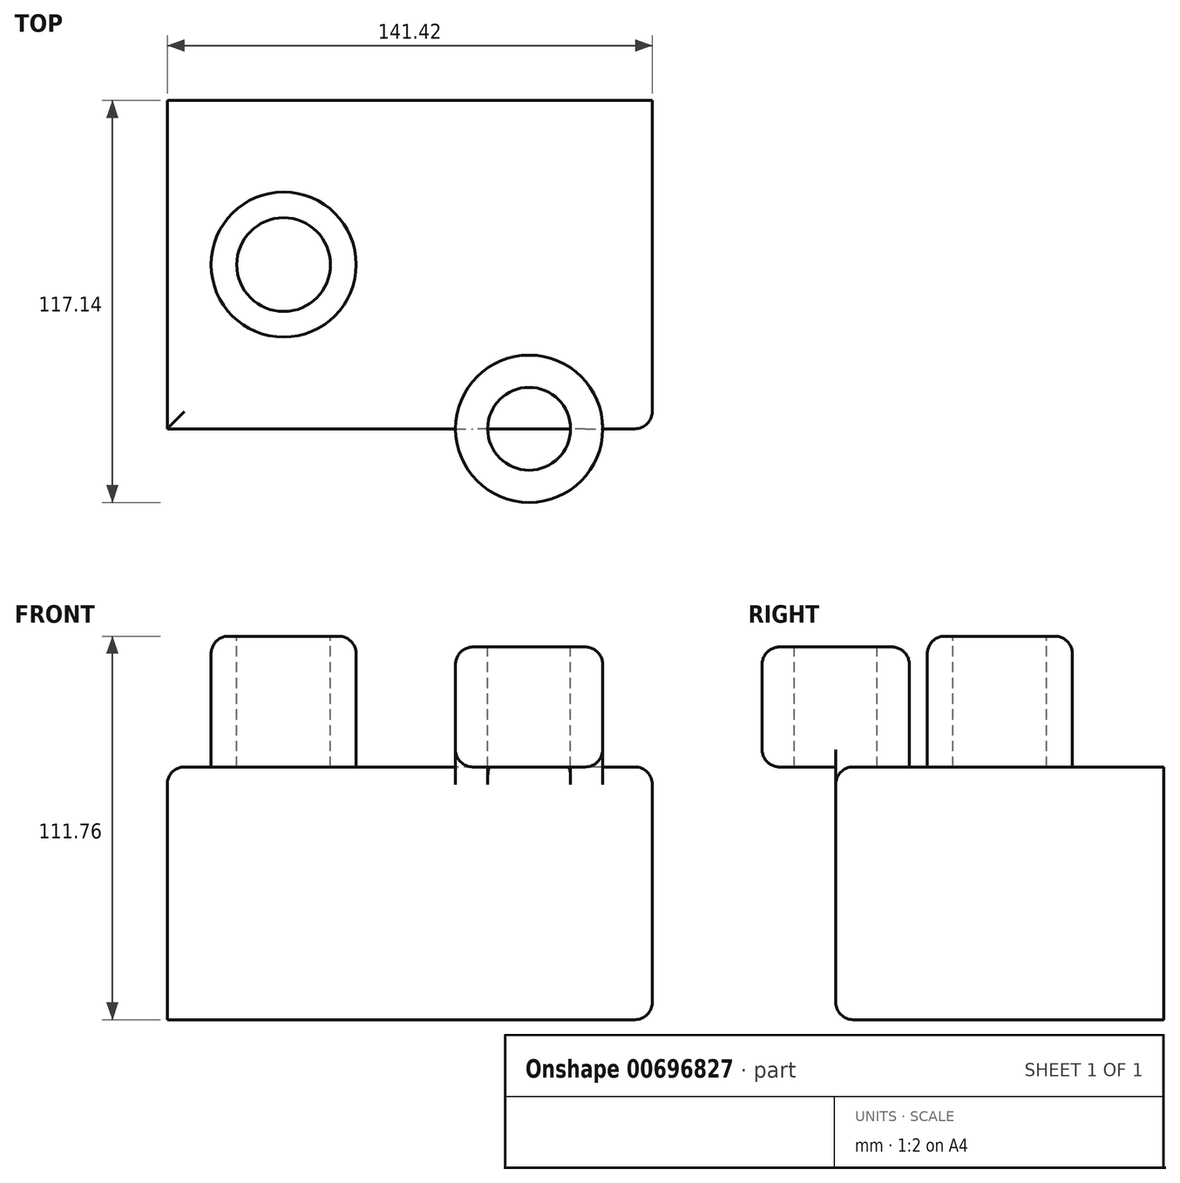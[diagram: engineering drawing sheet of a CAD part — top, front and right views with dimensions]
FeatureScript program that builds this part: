
annotation { "Feature Type Name" : "Feature", "Feature Type Description" : "" }
export const myFeature = defineFeature(function(context is Context, id is Id, definition is map)
    precondition{}
    {
        {
            var Q0;
            Q0=qCreatedBy(makeId("Top.planeOp"),FACE);
            var sketch = newSketch(context, id + "F0", { "sketchPlane" : qUnion([Q0])});
            skLineSegment(sketch, "E0.bottom", {"start": v(70.71, -47.84) * mm, "end": v(-70.71, -47.84) * mm});
            skLineSegment(sketch, "E0.top", {"start": v(70.71, 47.84) * mm, "end": v(-70.71, 47.84) * mm});
            skLineSegment(sketch, "E0.left", {"start": v(70.71, -47.84) * mm, "end": v(70.71, 47.84) * mm});
            skLineSegment(sketch, "E0.right", {"start": v(-70.71, -47.84) * mm, "end": v(-70.71, 47.84) * mm});
            skPoint(sketch, "E0.middle", {"position": v(0, 0) * mm});
            skSolve(sketch);
        }
        {
            var Q0;
            Q0 = qSketchRegion(id + "F0", true);
            extrude(context, id + "F1", {"entities" : qUnion([Q0]), "depth" : 73.66 * mm, "offsetDistance" : 25.4 * mm});
        }
        {
            var Q0;
            Q0=makeQuery(id+"F1.opExtrude","CAP_FACE",FACE,{"disambiguationData":[OSD([sQuery(id+"F0.wireOp",EDGE,"E0.bottom"),sQuery(id+"F0.wireOp",EDGE,"E0.top"),sQuery(id+"F0.wireOp",EDGE,"E0.left"),sQuery(id+"F0.wireOp",EDGE,"E0.right")])],"isStart":false});
            var sketch = newSketch(context, id + "F2", { "sketchPlane" : qUnion([Q0])});
            skCircle(sketch, "E1", {"center": v(-36.78, 0) * mm, "radius": 21.14 * mm});
            skSolve(sketch);
        }
        {
            var Q0;
            Q0=makeQuery(id+"F2.imprint","IMPRINT",FACE,{"disambiguationData":[TD([[makeQuery(id+"F2.imprint","IMPRINT",EDGE,{"derivedFrom":sQuery(id+"F2.wireOp",EDGE,"E1")}),1.0]])]});
            extrude(context, id + "F3", {"entities" : qUnion([Q0]), "operationType" : NewBodyOperationType.ADD, "depth" : 38.1 * mm, "offsetDistance" : 25.4 * mm});
        }
        {
            var Q0;
            Q0=makeQuery(id+"F3.opExtrude","CAP_FACE",FACE,{"disambiguationData":[OSD([sQuery(id+"F2.wireOp",EDGE,"E1")])],"isStart":false});
            var sketch = newSketch(context, id + "F4", { "sketchPlane" : qUnion([Q0])});
            skCircle(sketch, "E2", {"center": v(-36.78, 0) * mm, "radius": 13.66 * mm});
            skSolve(sketch);
        }
        {
            var Q0;
            Q0 = qSketchRegion(id + "F4", true);
            var Q1;
            Q1=makeQuery(id+"F1.opExtrude","CAP_FACE",FACE,{"disambiguationData":[OSD([sQuery(id+"F0.wireOp",EDGE,"E0.bottom"),sQuery(id+"F0.wireOp",EDGE,"E0.top"),sQuery(id+"F0.wireOp",EDGE,"E0.left"),sQuery(id+"F0.wireOp",EDGE,"E0.right")])],"isStart":false});
            extrude(context, id + "F5", {"entities" : qUnion([Q0]), "operationType" : NewBodyOperationType.REMOVE, "endBound" : BoundingType.UP_TO_SURFACE, "oppositeDirection" : true, "depth" : 25.4 * mm, "endBoundEntityFace" : qUnion([Q1]), "offsetDistance" : 25.4 * mm});
        }
        {
            var Q0;
            Q0=makeQuery(id+"F1.opExtrude","SWEPT_FACE",FACE,{"disambiguationData":[OSD([sQuery(id+"F0.wireOp",EDGE,"E0.bottom")])]});
            var sketch = newSketch(context, id + "F6", { "sketchPlane" : qUnion([Q0])});
            skLineSegment(sketch, "E3", {"start": v(34.8, 102.96) * mm, "end": v(34.8, 44.26) * mm});
            skLineSegment(sketch, "E4.bottom", {"start": v(13.33, 108.62) * mm, "end": v(22.72, 108.62) * mm});
            skLineSegment(sketch, "E4.top", {"start": v(13.33, 71.52) * mm, "end": v(22.72, 71.52) * mm});
            skLineSegment(sketch, "E4.left", {"start": v(13.33, 108.62) * mm, "end": v(13.33, 71.52) * mm});
            skLineSegment(sketch, "E4.right", {"start": v(22.72, 108.62) * mm, "end": v(22.72, 71.52) * mm});
            skSolve(sketch);
        }
        {
            var Q0;
            {var subQ0=sQuery(id+"F6.wireOp",EDGE,"E4.bottom");Q0=makeQuery(id+"F6.imprint","IMPRINT",FACE,{"disambiguationData":[TD([[makeQuery(id+"F6.imprint","IMPRINT",EDGE,{"derivedFrom":subQ0}),-1.0]])]});}
            var Q1;
            Q1=sQuery(id+"F6.wireOp",EDGE,"E3");
            revolve(context, id + "F7", {"operationType" : NewBodyOperationType.ADD, "entities" : qUnion([Q0]), "axis" : qUnion([Q1]), "revolveType" : RevolveType.FULL});
        }
        {
            var Q0;
            Q0=makeQuery(id+"F7.opRevolve","SWEPT_EDGE",EDGE,{"disambiguationData":[OSD([sQuery(id+"F6.wireOp",EDGE,"E4.bottom"),sQuery(id+"F6.wireOp",EDGE,"E4.left")])]});
            fillet(context, id + "F8", {"entities" : qUnion([Q0]), "radius" : 5.08 * mm, "tangentPropagation" : true, "allowEdgeOverflow" : false});
        }
        {
            var Q0;
            Q0=makeQuery(id+"F3.opExtrude","CAP_EDGE",EDGE,{"disambiguationData":[OSD([sQuery(id+"F2.wireOp",EDGE,"E1")])],"isStart":false});
            fillet(context, id + "F9", {"entities" : qUnion([Q0]), "radius" : 5.08 * mm, "tangentPropagation" : true, "allowEdgeOverflow" : false});
        }
        {
            var Q0;
            Q0=makeQuery(id+"F1.opExtrude","CAP_EDGE",EDGE,{"disambiguationData":[OSD([sQuery(id+"F0.wireOp",EDGE,"E0.left")])],"isStart":false});
            var Q1;
            Q1=makeQuery(id+"F1.opExtrude","CAP_EDGE",EDGE,{"disambiguationData":[OSD([sQuery(id+"F0.wireOp",EDGE,"E0.left")])],"isStart":true});
            fillet(context, id + "F10", {"entities" : qUnion([Q0, Q1]), "radius" : 5.08 * mm, "tangentPropagation" : true, "allowEdgeOverflow" : false});
        }
        {
            var Q0;
            {var subQ0=sQuery(id+"F6.wireOp",EDGE,"E4.left");var subQ1=sQuery(id+"F0.wireOp",EDGE,"E0.bottom");Q0=makeQuery(id+"F7.boolean.opBoolean","SPLIT",EDGE,{"disambiguationData":[topologyDisambiguationEdgeConnected([makeQuery(id+"F7.opRevolve","SWEPT_FACE",FACE,{"disambiguationData":[OSD([subQ1])]})])],"derivedFrom":makeQuery(id+"F7.opRevolve","SWEPT_EDGE",EDGE,{"disambiguationData":[OSD([subQ1,subQ0])]})});}
            fillet(context, id + "F11", {"entities" : qUnion([Q0]), "radius" : 5.08 * mm, "tangentPropagation" : true, "allowEdgeOverflow" : false});
        }
        {
            var Q0;
            {var subQ0=sQuery(id+"F0.wireOp",EDGE,"E0.right");var subQ1=sQuery(id+"F0.wireOp",EDGE,"E0.bottom");var subQ2=makeQuery(id+"F1.opExtrude","CAP_FACE",FACE,{"disambiguationData":[OSD([subQ1,sQuery(id+"F0.wireOp",EDGE,"E0.top"),sQuery(id+"F0.wireOp",EDGE,"E0.left"),subQ0])],"isStart":false});var subQ3=makeQuery(id+"F1.opExtrude","SWEPT_FACE",FACE,{"disambiguationData":[OSD([subQ1])]});Q0=makeQuery(id+"F7.boolean.opBoolean","SPLIT",EDGE,{"disambiguationData":[topologyDisambiguationEdgeConnected([subQ3,subQ2]),TD([makeQuery(id+"F1.opExtrude","SWEPT_FACE",FACE,{"disambiguationData":[OSD([subQ0])]})])],"derivedFrom":makeQuery(id+"F1.opExtrude","CAP_EDGE",EDGE,{"disambiguationData":[OSD([subQ1])],"isStart":false})});}
            var Q1;
            Q1=makeQuery(id+"F1.opExtrude","CAP_EDGE",EDGE,{"disambiguationData":[OSD([sQuery(id+"F0.wireOp",EDGE,"E0.right")])],"isStart":false});
            fillet(context, id + "F12", {"entities" : qUnion([Q0, Q1]), "radius" : 5.08 * mm, "tangentPropagation" : true, "allowEdgeOverflow" : false});
        }
    });
